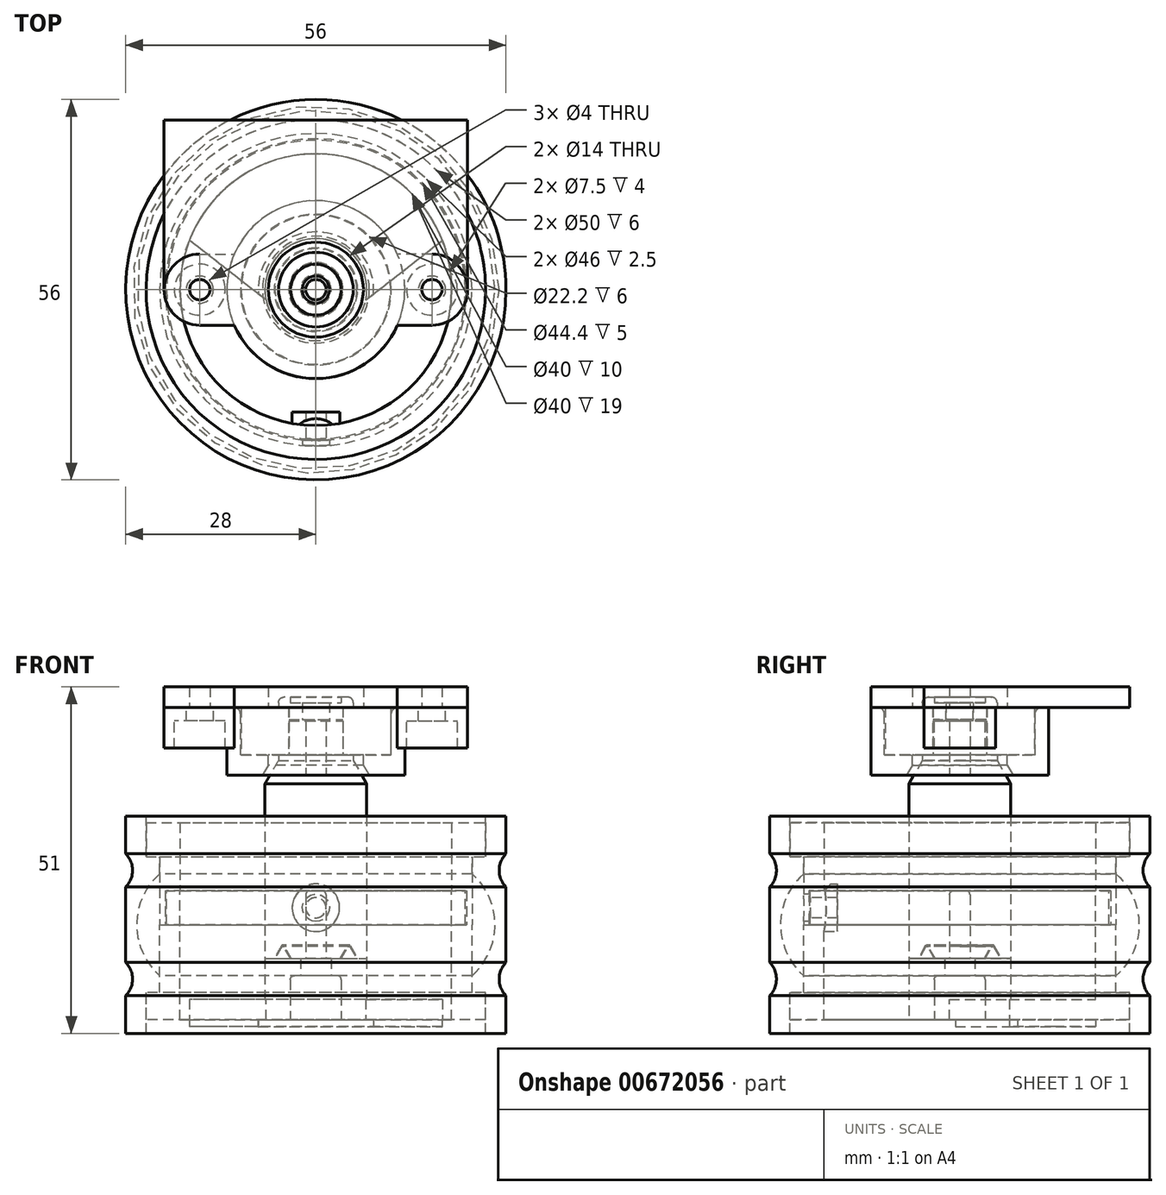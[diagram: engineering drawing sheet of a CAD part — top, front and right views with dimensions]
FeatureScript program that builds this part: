
annotation { "Feature Type Name" : "Feature", "Feature Type Description" : "" }
export const myFeature = defineFeature(function(context is Context, id is Id, definition is map)
    precondition{}
    {
        {
            var Q0;
            Q0=qCreatedBy(makeId("Top.planeOp"),FACE);
            var sketch = newSketch(context, id + "F0", { "sketchPlane" : qUnion([Q0])});
            skCircle(sketch, "E0", {"center": v(0, 0) * mm, "radius": 11.07 * mm});
            skCircle(sketch, "E1", {"center": v(0, 0) * mm, "radius": 13.75 * mm});
            skCircle(sketch, "E2", {"center": v(0, 0) * mm, "radius": 20 * mm});
            skCircle(sketch, "E3", {"center": v(0, 0) * mm, "radius": 25 * mm});
            skCircle(sketch, "E4", {"center": v(0, 0) * mm, "radius": 7.5 * mm});
            skSolve(sketch);
        }
        {
            var Q0;
            Q0=qCreatedBy(makeId("Front.planeOp"),FACE);
            var sketch = newSketch(context, id + "F1", { "sketchPlane" : qUnion([Q0])});
            skPoint(sketch, "E5.0", {"position": v(0, 0) * mm});
            skLineSegment(sketch, "E6", {"start": v(20, 30) * mm, "end": v(20, 0) * mm, "construction": true});
            skLineSegment(sketch, "E7", {"start": v(25, 30) * mm, "end": v(25, 0) * mm, "construction": true});
            skLineSegment(sketch, "E8", {"start": v(25, 30) * mm, "end": v(25, 25) * mm});
            skLineSegment(sketch, "E9", {"start": v(25, 25) * mm, "end": v(23, 25) * mm});
            skLineSegment(sketch, "E10", {"start": v(23, 25) * mm, "end": v(23, 15) * mm});
            skLineSegment(sketch, "E11", {"start": v(25, 30) * mm, "end": v(20, 30) * mm});
            skLineSegment(sketch, "E12", {"start": v(20, 15) * mm, "end": v(20, 30) * mm});
            skLineSegment(sketch, "E13", {"start": v(20, 15) * mm, "end": v(23, 15) * mm});
            skLineSegment(sketch, "E14.MirrorCS", {"start": v(23, 5) * mm, "end": v(23, 15) * mm});
            skLineSegment(sketch, "E15.MirrorCS", {"start": v(25, 0) * mm, "end": v(25, 5) * mm});
            skLineSegment(sketch, "E16.MirrorCS", {"start": v(25, 5) * mm, "end": v(23, 5) * mm});
            skLineSegment(sketch, "E17.MirrorCS", {"start": v(25, 0) * mm, "end": v(20, 0) * mm});
            skLineSegment(sketch, "E18.MirrorCS", {"start": v(20, 15) * mm, "end": v(20, 0) * mm});
            skLineSegment(sketch, "E19", {"start": v(25, 25) * mm, "end": v(25, 5) * mm});
            skSolve(sketch);
        }
        {
            var Q0;
            Q0=qCreatedBy(makeId("Front.planeOp"),FACE);
            var sketch = newSketch(context, id + "F2", { "sketchPlane" : qUnion([Q0])});
            skLineSegment(sketch, "E20.0.0", {"start": v(23, 15) * mm, "end": v(20, 15) * mm});
            skLineSegment(sketch, "E20.0.1", {"start": v(20, 15) * mm, "end": v(20, 0) * mm});
            skLineSegment(sketch, "E20.0.2", {"start": v(20, 0) * mm, "end": v(25, 0) * mm});
            skLineSegment(sketch, "E20.0.3", {"start": v(25, 0) * mm, "end": v(25, 5) * mm});
            skLineSegment(sketch, "E20.0.4", {"start": v(25, 5) * mm, "end": v(23, 5) * mm});
            skLineSegment(sketch, "E20.0.5", {"start": v(23, 5) * mm, "end": v(23, 15) * mm});
            skLineSegment(sketch, "E21", {"start": v(20, 15) * mm, "end": v(20, 20) * mm});
            skLineSegment(sketch, "E22", {"start": v(20, 20) * mm, "end": v(22, 20) * mm});
            skLineSegment(sketch, "E23", {"start": v(22, 20) * mm, "end": v(22, 15) * mm});
            skSolve(sketch);
        }
        {
            var Q0;
            Q0=qCreatedBy(makeId("Front.planeOp"),FACE);
            var sketch = newSketch(context, id + "F3", { "sketchPlane" : qUnion([Q0])});
            skLineSegment(sketch, "E24.0.0", {"start": v(20, 30) * mm, "end": v(20, 15) * mm});
            skLineSegment(sketch, "E24.0.1", {"start": v(20, 15) * mm, "end": v(23, 15) * mm});
            skLineSegment(sketch, "E24.0.2", {"start": v(23, 15) * mm, "end": v(23, 25) * mm});
            skLineSegment(sketch, "E24.0.3", {"start": v(23, 25) * mm, "end": v(25, 25) * mm});
            skLineSegment(sketch, "E24.0.4", {"start": v(25, 25) * mm, "end": v(25, 30) * mm});
            skLineSegment(sketch, "E24.0.5", {"start": v(25, 30) * mm, "end": v(20, 30) * mm});
            skLineSegment(sketch, "E25.0", {"start": v(22.2, 20) * mm, "end": v(22.2, 15) * mm});
            skLineSegment(sketch, "E26.0", {"start": v(20, 20) * mm, "end": v(22, 20) * mm, "construction": true});
            skLineSegment(sketch, "E27", {"start": v(20, 20) * mm, "end": v(22.2, 20) * mm});
            skSolve(sketch);
        }
        {
            var Q0;
            Q0=qCreatedBy(makeId("Top.planeOp"),FACE);
            var sketch = newSketch(context, id + "F4", { "sketchPlane" : qUnion([Q0])});
            skCircle(sketch, "E28", {"center": v(0, 0) * mm, "radius": 2.25 * mm});
            skCircle(sketch, "E29", {"center": v(0, 0) * mm, "radius": 3.75 * mm});
            skCircle(sketch, "E30", {"center": v(0, 0) * mm, "radius": 7.5 * mm});
            skSolve(sketch);
        }
        {
            var Q0;
            Q0=makeQuery(id+"F4.imprint","IMPRINT",FACE,{"disambiguationData":[TD([[makeQuery(id+"F4.imprint","IMPRINT",EDGE,{"derivedFrom":sQuery(id+"F4.wireOp",EDGE,"E29")}),-1.0]])]});
            var Q1;
            Q1=makeQuery(id+"F4.imprint","IMPRINT",FACE,{"disambiguationData":[TD([[makeQuery(id+"F4.imprint","IMPRINT",EDGE,{"derivedFrom":sQuery(id+"F4.wireOp",EDGE,"E28")}),-1.0]])]});
            extrude(context, id + "F5", {"entities" : qUnion([Q0, Q1]), "depth" : 10 * mm, "offsetDistance" : 25 * mm});
        }
        {
            var Q0;
            Q0=makeQuery(id+"F4.imprint","IMPRINT",FACE,{"disambiguationData":[TD([[makeQuery(id+"F4.imprint","IMPRINT",EDGE,{"derivedFrom":sQuery(id+"F4.wireOp",EDGE,"E28")}),-1.0]])]});
            extrude(context, id + "F6", {"entities" : qUnion([Q0]), "operationType" : NewBodyOperationType.REMOVE, "depth" : 7.5 * mm, "offsetDistance" : 25 * mm});
        }
        {
            var Q0;
            Q0=qCreatedBy(makeId("Front.planeOp"),FACE);
            var sketch = newSketch(context, id + "F7", { "sketchPlane" : qUnion([Q0])});
            skLineSegment(sketch, "E31.0.0", {"start": v(-7.5, 10) * mm, "end": v(7.5, 10) * mm});
            skLineSegment(sketch, "E32.0", {"start": v(-20, 0) * mm, "end": v(20, 0) * mm});
            skLineSegment(sketch, "E33", {"start": v(-7.5, 0) * mm, "end": v(-7.5, 10) * mm});
            skLineSegment(sketch, "E34", {"start": v(7.5, 10) * mm, "end": v(7.5, 0) * mm});
            skLineSegment(sketch, "E35", {"start": v(-2.25, 7.5) * mm, "end": v(-2.25, 10) * mm});
            skLineSegment(sketch, "E36", {"start": v(2.25, 10) * mm, "end": v(2.25, 7.5) * mm});
            skLineSegment(sketch, "E37", {"start": v(-2.25, 10) * mm, "end": v(-7.5, 10) * mm});
            skLineSegment(sketch, "E38", {"start": v(-4.88, 10) * mm, "end": v(-4.88, 12) * mm, "construction": true});
            skLineSegment(sketch, "E39", {"start": v(-4.88, 12) * mm, "end": v(-6.03, 10) * mm});
            skLineSegment(sketch, "E40.MirrorCS", {"start": v(-4.88, 12) * mm, "end": v(-3.72, 10) * mm});
            skSolve(sketch);
        }
        {
            var Q0;
            {var subQ0=sQuery(id+"F7.wireOp",EDGE,"E39");Q0=makeQuery(id+"F7.imprint","IMPRINT",FACE,{"disambiguationData":[TD([[makeQuery(id+"F7.imprint","IMPRINT",EDGE,{"derivedFrom":subQ0}),1.0]])]});}
            var Q1;
            Q1=makeQuery(id+"F5.opExtrude","SWEPT_FACE",FACE,{"disambiguationData":[OSD([sQuery(id+"F4.wireOp",EDGE,"E28")])]});
            revolve(context, id + "F8", {"operationType" : NewBodyOperationType.ADD, "entities" : qUnion([Q0]), "axis" : qUnion([Q1]), "revolveType" : RevolveType.FULL});
        }
        {
            var Q0;
            Q0=qCreatedBy(makeId("Front.planeOp"),FACE);
            var sketch = newSketch(context, id + "F9", { "sketchPlane" : qUnion([Q0])});
            skLineSegment(sketch, "E41.0", {"start": v(-7.5, 10) * mm, "end": v(7.5, 10) * mm});
            skLineSegment(sketch, "E42", {"start": v(0, 0) * mm, "end": v(0, 10) * mm, "construction": true});
            skLineSegment(sketch, "E43", {"start": v(0, 10) * mm, "end": v(0, 45) * mm});
            skLineSegment(sketch, "E44", {"start": v(7.5, 10) * mm, "end": v(7.5, 45) * mm});
            skLineSegment(sketch, "E45", {"start": v(7.5, 45) * mm, "end": v(0, 45) * mm});
            skLineSegment(sketch, "E46", {"start": v(7.5, 45) * mm, "end": v(7.5, 40) * mm, "construction": true});
            skLineSegment(sketch, "E47", {"start": v(7.5, 40) * mm, "end": v(0, 40) * mm, "construction": true});
            skLineSegment(sketch, "E48", {"start": v(0, 40) * mm, "end": v(3.95, 40) * mm, "construction": true});
            skLineSegment(sketch, "E49", {"start": v(3.95, 40) * mm, "end": v(3.95, 45) * mm});
            skLineSegment(sketch, "E50", {"start": v(3.95, 40) * mm, "end": v(7.5, 40) * mm});
            skLineSegment(sketch, "E51", {"start": v(0, 10) * mm, "end": v(0, 20) * mm, "construction": true});
            skLineSegment(sketch, "E52", {"start": v(0, 20) * mm, "end": v(1.5, 20) * mm});
            skLineSegment(sketch, "E53", {"start": v(1.5, 20) * mm, "end": v(1.5, 10) * mm});
            skLineSegment(sketch, "E54", {"start": v(1.5, 10) * mm, "end": v(0, 10) * mm});
            skLineSegment(sketch, "E55", {"start": v(0, 45) * mm, "end": v(1.5, 45) * mm});
            skLineSegment(sketch, "E56", {"start": v(1.5, 45) * mm, "end": v(1.5, 40) * mm});
            skLineSegment(sketch, "E57", {"start": v(1.5, 40) * mm, "end": v(0, 40) * mm});
            skLineSegment(sketch, "E58", {"start": v(4.88, 12) * mm, "end": v(3.72, 10) * mm});
            skLineSegment(sketch, "E59", {"start": v(-6.03, 10) * mm, "end": v(-4.88, 12) * mm});
            skLineSegment(sketch, "E60", {"start": v(4.88, 12) * mm, "end": v(6.03, 10) * mm});
            skLineSegment(sketch, "E61.0.0", {"start": v(-3.72, 10) * mm, "end": v(3.72, 10) * mm});
            skLineSegment(sketch, "E62.0", {"start": v(4.88, 12.2) * mm, "end": v(3.6, 10) * mm});
            skLineSegment(sketch, "E62.1", {"start": v(4.88, 12.2) * mm, "end": v(6.15, 10) * mm});
            skLineSegment(sketch, "E63", {"start": v(7.5, 45) * mm, "end": v(7.5, 45.2) * mm, "construction": true});
            skLineSegment(sketch, "E64", {"start": v(7.5, 45.2) * mm, "end": v(0, 45.2) * mm, "construction": true});
            skLineSegment(sketch, "E65", {"start": v(0, 40) * mm, "end": v(5.5, 40) * mm});
            skLineSegment(sketch, "E66", {"start": v(5.5, 40) * mm, "end": v(5.5, 39.2) * mm});
            skLineSegment(sketch, "E67", {"start": v(5.5, 39.2) * mm, "end": v(7.5, 39.2) * mm});
            skLineSegment(sketch, "E68", {"start": v(3.95, 45) * mm, "end": v(3.95, 45.2) * mm, "construction": true});
            skLineSegment(sketch, "E69", {"start": v(3.95, 45.2) * mm, "end": v(3.95, 47) * mm});
            skLineSegment(sketch, "E70", {"start": v(5.5, 40) * mm, "end": v(5.5, 47) * mm, "construction": true});
            skLineSegment(sketch, "E71", {"start": v(5.5, 47) * mm, "end": v(3.95, 47) * mm});
            skLineSegment(sketch, "E72", {"start": v(5.5, 47) * mm, "end": v(5.5, 48.5) * mm});
            skLineSegment(sketch, "E73", {"start": v(5.5, 48.5) * mm, "end": v(0, 48.5) * mm});
            skLineSegment(sketch, "E74", {"start": v(0, 48.5) * mm, "end": v(0, 45.2) * mm});
            skLineSegment(sketch, "E75", {"start": v(3.95, 45.2) * mm, "end": v(0, 45.2) * mm});
            skLineSegment(sketch, "E76", {"start": v(0, 48.5) * mm, "end": v(1.88, 48.5) * mm});
            skLineSegment(sketch, "E77", {"start": v(0, 45.2) * mm, "end": v(2, 45.2) * mm, "construction": true});
            skLineSegment(sketch, "E78", {"start": v(2, 45.2) * mm, "end": v(2, 47.7) * mm});
            skLineSegment(sketch, "E79", {"start": v(0, 48.5) * mm, "end": v(3.75, 48.5) * mm, "construction": true});
            skLineSegment(sketch, "E80", {"start": v(3.75, 48.5) * mm, "end": v(3.75, 47.7) * mm});
            skLineSegment(sketch, "E81", {"start": v(3.75, 47.7) * mm, "end": v(2, 47.7) * mm});
            skLineSegment(sketch, "E82", {"start": v(5.5, 39.2) * mm, "end": v(7.5, 35.74) * mm});
            skLineSegment(sketch, "E83", {"start": v(1.5, 40) * mm, "end": v(1.5, 37) * mm});
            skLineSegment(sketch, "E84", {"start": v(1.5, 37) * mm, "end": v(0, 37) * mm});
            skSolve(sketch);
        }
        {
            var Q0;
            {var subQ4=sQuery(id+"F9.wireOp",EDGE,"E52");Q0=makeQuery(id+"F9.imprint","IMPRINT",FACE,{"disambiguationData":[TD([[makeQuery(id+"F9.imprint","IMPRINT",EDGE,{"derivedFrom":subQ4}),1.0]])]});}
            var Q1;
            {var subQ2=sQuery(id+"F9.wireOp",EDGE,"E49");Q1=makeQuery(id+"F9.imprint","IMPRINT",FACE,{"disambiguationData":[TD([[makeQuery(id+"F9.imprint","IMPRINT",EDGE,{"derivedFrom":subQ2}),1.0]])]});}
            var Q2;
            {var subQ3=sQuery(id+"F9.wireOp",EDGE,"E69");Q2=makeQuery(id+"F9.imprint","IMPRINT",FACE,{"disambiguationData":[TD([[makeQuery(id+"F9.imprint","IMPRINT",EDGE,{"derivedFrom":subQ3}),1.0]])]});}
            var Q3;
            Q3=sQuery(id+"F9.wireOp",EDGE,"E43");
            revolve(context, id + "F10", {"entities" : qUnion([Q0, Q1, Q2]), "axis" : qUnion([Q3]), "revolveType" : RevolveType.FULL});
        }
        {
            var Q0;
            Q0=makeQuery(id+"F8.opRevolve","SWEPT_EDGE",EDGE,{"disambiguationData":[OSD([sQuery(id+"F7.wireOp",EDGE,"E39"),sQuery(id+"F7.wireOp",EDGE,"E40.MirrorCS")])]});
            var Q1;
            Q1=makeQuery(id+"F10.opRevolve","SWEPT_EDGE",EDGE,{"disambiguationData":[OSD([sQuery(id+"F9.wireOp",EDGE,"E62.0"),sQuery(id+"F9.wireOp",EDGE,"E62.1")])]});
            fillet(context, id + "F11", {"entities" : qUnion([Q0, Q1]), "radius" : .2 * mm, "tangentPropagation" : true, "allowEdgeOverflow" : false});
        }
        {
            var Q0;
            Q0=makeQuery(id+"F10.opRevolve","SWEPT_EDGE",EDGE,{"disambiguationData":[OSD([sQuery(id+"F9.wireOp",EDGE,"E52"),sQuery(id+"F9.wireOp",EDGE,"E53")])]});
            var Q1;
            Q1=makeQuery(id+"F6.boolean.opBoolean","COPY",EDGE,{"derivedFrom":makeQuery(id+"F6.opExtrude","CAP_EDGE",EDGE,{"disambiguationData":[OSD([sQuery(id+"F4.wireOp",EDGE,"E28")])],"isStart":false})});
            var Q2;
            Q2=makeQuery(id+"F6.boolean.opBoolean","COPY",EDGE,{"derivedFrom":makeQuery(id+"F6.opExtrude","CAP_EDGE",EDGE,{"disambiguationData":[OSD([sQuery(id+"F4.wireOp",EDGE,"E29")])],"isStart":false})});
            fillet(context, id + "F12", {"entities" : qUnion([Q0, Q1, Q2]), "radius" : .6 * mm, "tangentPropagation" : true, "allowEdgeOverflow" : false});
        }
        {
            var Q0;
            Q0=makeQuery(id+"F10.opRevolve","SWEPT_EDGE",EDGE,{"disambiguationData":[OSD([sQuery(id+"F9.wireOp",EDGE,"E72"),sQuery(id+"F9.wireOp",EDGE,"E73")])]});
            fillet(context, id + "F13", {"entities" : qUnion([Q0]), "radius" : .8 * mm, "tangentPropagation" : true, "allowEdgeOverflow" : false});
        }
        {
            var Q0;
            Q0=qCreatedBy(makeId("Front.planeOp"),FACE);
            var sketch = newSketch(context, id + "F14", { "sketchPlane" : qUnion([Q0])});
            skLineSegment(sketch, "E85.0.0", {"start": v(-5.5, 40) * mm, "end": v(5.5, 40) * mm, "construction": true});
            skLineSegment(sketch, "E86", {"start": v(-3.95, 40) * mm, "end": v(-3.95, 45) * mm, "construction": true});
            skLineSegment(sketch, "E87", {"start": v(3.95, 45) * mm, "end": v(3.95, 40) * mm, "construction": true});
            skLineSegment(sketch, "E88.0.0", {"start": v(5.5, 47) * mm, "end": v(-5.5, 47) * mm, "construction": true});
            skLineSegment(sketch, "E89", {"start": v(-3.95, 45.2) * mm, "end": v(-3.95, 47) * mm, "construction": true});
            skLineSegment(sketch, "E90", {"start": v(3.95, 47) * mm, "end": v(3.95, 45.2) * mm, "construction": true});
            skLineSegment(sketch, "E91", {"start": v(-5.5, 47) * mm, "end": v(-5.5, 40) * mm});
            skLineSegment(sketch, "E92", {"start": v(0, 40) * mm, "end": v(0, 47) * mm, "construction": true});
            skLineSegment(sketch, "E93", {"start": v(0, 43.5) * mm, "end": v(-11, 43.5) * mm, "construction": true});
            skLineSegment(sketch, "E94", {"start": v(-11, 43.5) * mm, "end": v(-11, 47) * mm});
            skLineSegment(sketch, "E95", {"start": v(-11, 47) * mm, "end": v(-5.5, 47) * mm});
            skLineSegment(sketch, "E96", {"start": v(-11, 43.5) * mm, "end": v(-11, 40) * mm});
            skLineSegment(sketch, "E97", {"start": v(-11, 40) * mm, "end": v(-5.5, 40) * mm});
            skLineSegment(sketch, "E98", {"start": v(-3.95, 40) * mm, "end": v(-3.95, 47) * mm});
            skLineSegment(sketch, "E99", {"start": v(0, 43.5) * mm, "end": v(-4, 43.5) * mm, "construction": true});
            skLineSegment(sketch, "E100", {"start": v(-4, 43.5) * mm, "end": v(-4, 47) * mm});
            skLineSegment(sketch, "E101", {"start": v(-4, 47) * mm, "end": v(-5.5, 47) * mm});
            skLineSegment(sketch, "E102", {"start": v(-4, 43.5) * mm, "end": v(-4, 40) * mm});
            skLineSegment(sketch, "E103", {"start": v(-4, 40) * mm, "end": v(-5.5, 40) * mm});
            skSolve(sketch);
        }
        {
            var Q0;
            Q0=makeQuery(id+"F14.imprint","IMPRINT",FACE,{"disambiguationData":[TD([[makeQuery(id+"F14.imprint","IMPRINT",EDGE,{"derivedFrom":sQuery(id+"F14.wireOp",EDGE,"E91")}),-1.0]])]});
            var Q1;
            Q1=makeQuery(id+"F14.imprint","IMPRINT",FACE,{"disambiguationData":[TD([[makeQuery(id+"F14.imprint","IMPRINT",EDGE,{"derivedFrom":sQuery(id+"F14.wireOp",EDGE,"E91")}),1.0]])]});
            var Q2;
            Q2=sQuery(id+"F14.wireOp",EDGE,"E92");
            revolve(context, id + "F15", {"entities" : qUnion([Q0, Q1]), "axis" : qUnion([Q2]), "revolveType" : RevolveType.FULL});
        }
        {
            var Q0;
            Q0=qCreatedBy(makeId("Front.planeOp"),FACE);
            var sketch = newSketch(context, id + "F16", { "sketchPlane" : qUnion([Q0])});
            skLineSegment(sketch, "E104", {"start": v(-1.5, 40) * mm, "end": v(-1.5, 45) * mm, "construction": true});
            skLineSegment(sketch, "E105", {"start": v(1.5, 45) * mm, "end": v(1.5, 40) * mm, "construction": true});
            skLineSegment(sketch, "E106.0.0", {"start": v(3.95, 40) * mm, "end": v(-3.95, 40) * mm, "construction": true});
            skLineSegment(sketch, "E107.0.0", {"start": v(-3.95, 45) * mm, "end": v(3.95, 45) * mm, "construction": true});
            skLineSegment(sketch, "E108", {"start": v(0, 45) * mm, "end": v(0, 40) * mm, "construction": true});
            skLineSegment(sketch, "E109.0.0", {"start": v(11, 40) * mm, "end": v(-11, 40) * mm, "construction": true});
            skLineSegment(sketch, "E110", {"start": v(-11, 40) * mm, "end": v(-11, 47) * mm, "construction": true});
            skLineSegment(sketch, "E111", {"start": v(11, 47) * mm, "end": v(11, 40) * mm, "construction": true});
            skLineSegment(sketch, "E112", {"start": v(-7.5, 35.74) * mm, "end": v(-5.5, 39.2) * mm, "construction": true});
            skLineSegment(sketch, "E113", {"start": v(5.5, 39.2) * mm, "end": v(7.5, 35.74) * mm, "construction": true});
            skLineSegment(sketch, "E114", {"start": v(-5.5, 39.2) * mm, "end": v(-5.5, 40) * mm, "construction": true});
            skLineSegment(sketch, "E115", {"start": v(5.5, 40) * mm, "end": v(5.5, 39.2) * mm, "construction": true});
            skLineSegment(sketch, "E116", {"start": v(-5.5, 40) * mm, "end": v(-7, 40) * mm, "construction": true});
            skLineSegment(sketch, "E117", {"start": v(-7, 40) * mm, "end": v(-7, 38.5) * mm});
            skLineSegment(sketch, "E118", {"start": v(0, 40) * mm, "end": v(-11.1, 40) * mm});
            skLineSegment(sketch, "E119", {"start": v(-11.1, 40) * mm, "end": v(-11.1, 47.44) * mm});
            skLineSegment(sketch, "E120", {"start": v(-11.1, 47) * mm, "end": v(-13.1, 47) * mm});
            skLineSegment(sketch, "E121", {"start": v(-7, 38.5) * mm, "end": v(-7.87, 37) * mm});
            skLineSegment(sketch, "E122", {"start": v(-7.87, 37) * mm, "end": v(-13.1, 37) * mm});
            skLineSegment(sketch, "E123", {"start": v(-13.1, 37) * mm, "end": v(-13.1, 47) * mm});
            skLineSegment(sketch, "E124", {"start": v(-13.1, 47) * mm, "end": v(-21.1, 47) * mm});
            skLineSegment(sketch, "E125", {"start": v(-21.1, 47) * mm, "end": v(-21.1, 44) * mm});
            skLineSegment(sketch, "E126", {"start": v(-21.1, 44) * mm, "end": v(-13.1, 44) * mm});
            skSolve(sketch);
        }
        {
            var Q0;
            {var subQ4=sQuery(id+"F16.wireOp",EDGE,"E117");Q0=makeQuery(id+"F16.imprint","IMPRINT",FACE,{"disambiguationData":[TD([[makeQuery(id+"F16.imprint","IMPRINT",EDGE,{"derivedFrom":subQ4}),-1.0]])]});}
            var Q1;
            Q1=sQuery(id+"F16.wireOp",EDGE,"E108");
            revolve(context, id + "F17", {"entities" : qUnion([Q0]), "axis" : qUnion([Q1]), "revolveType" : RevolveType.FULL});
        }
        {
            var Q0;
            Q0=makeQuery(id+"F17.opRevolve","SWEPT_FACE",FACE,{"disambiguationData":[OSD([sQuery(id+"F16.wireOp",EDGE,"E120")])]});
            var sketch = newSketch(context, id + "F18", { "sketchPlane" : qUnion([Q0])});
            skCircle(sketch, "E127.0", {"center": v(0, 0) * mm, "radius": 13.1 * mm, "construction": true});
            skLineSegment(sketch, "E128.0", {"start": v(-21.1, 0) * mm, "end": v(-13.1, 0) * mm, "construction": true});
            skCircle(sketch, "E129", {"center": v(-17.1, 0) * mm, "radius": 3.75 * mm});
            skCircle(sketch, "E130", {"center": v(-17.1, 0) * mm, "radius": 2 * mm});
            skCircle(sketch, "E131", {"center": v(-17.1, 0) * mm, "radius": 5.25 * mm});
            skLineSegment(sketch, "E132", {"start": v(-17.1, 0) * mm, "end": v(-17.1, 5.25) * mm, "construction": true});
            skLineSegment(sketch, "E133", {"start": v(-17.1, 0) * mm, "end": v(-17.1, -5.25) * mm, "construction": true});
            skLineSegment(sketch, "E134", {"start": v(-17.1, -5.25) * mm, "end": v(-12, -5.25) * mm});
            skLineSegment(sketch, "E135", {"start": v(-17.1, 5.25) * mm, "end": v(-12, 5.25) * mm});
            skLineSegment(sketch, "E136", {"start": v(0, 0) * mm, "end": v(0, 7.47) * mm});
            skCircle(sketch, "E137.MirrorC", {"center": v(17.1, 0) * mm, "radius": 5.25 * mm});
            skCircle(sketch, "E138.MirrorC", {"center": v(17.1, 0) * mm, "radius": 2 * mm});
            skCircle(sketch, "E139.MirrorC", {"center": v(17.1, 0) * mm, "radius": 3.75 * mm});
            skLineSegment(sketch, "E140.MirrorCS", {"start": v(17.1, 5.25) * mm, "end": v(12, 5.25) * mm});
            skLineSegment(sketch, "E141.MirrorCS", {"start": v(17.1, -5.25) * mm, "end": v(12, -5.25) * mm});
            skSolve(sketch);
        }
        {
            var Q0;
            Q0=makeQuery(id+"F18.imprint","IMPRINT",FACE,{"disambiguationData":[TD([[makeQuery(id+"F18.imprint","IMPRINT",EDGE,{"derivedFrom":sQuery(id+"F18.wireOp",EDGE,"E129")}),1.0]])]});
            var Q1;
            Q1=makeQuery(id+"F18.imprint","IMPRINT",FACE,{"disambiguationData":[TD([[makeQuery(id+"F18.imprint","IMPRINT",EDGE,{"derivedFrom":sQuery(id+"F18.wireOp",EDGE,"E129")}),-1.0]])]});
            var Q2;
            {var subQ0=sQuery(id+"F18.wireOp",EDGE,"E134");Q2=makeQuery(id+"F18.imprint","IMPRINT",FACE,{"disambiguationData":[TD([[makeQuery(id+"F18.imprint","IMPRINT",EDGE,{"derivedFrom":subQ0}),1.0]])]});}
            var Q3;
            {var subQ0=sQuery(id+"F18.wireOp",EDGE,"E135");Q3=makeQuery(id+"F18.imprint","IMPRINT",FACE,{"disambiguationData":[TD([[makeQuery(id+"F18.imprint","IMPRINT",EDGE,{"derivedFrom":subQ0}),-1.0]])]});}
            extrude(context, id + "F19", {"entities" : qUnion([Q0, Q1, Q2, Q3]), "oppositeDirection" : true, "depth" : 2 * mm, "offsetDistance" : 25 * mm});
        }
        {
            var Q0;
            Q0=makeQuery(id+"F18.imprint","IMPRINT",FACE,{"disambiguationData":[TD([[makeQuery(id+"F18.imprint","IMPRINT",EDGE,{"derivedFrom":sQuery(id+"F18.wireOp",EDGE,"E129")}),-1.0]])]});
            var Q1;
            {var subQ0=sQuery(id+"F18.wireOp",EDGE,"E135");Q1=makeQuery(id+"F18.imprint","IMPRINT",FACE,{"disambiguationData":[TD([[makeQuery(id+"F18.imprint","IMPRINT",EDGE,{"derivedFrom":subQ0}),-1.0]])]});}
            var Q2;
            {var subQ0=sQuery(id+"F18.wireOp",EDGE,"E134");Q2=makeQuery(id+"F18.imprint","IMPRINT",FACE,{"disambiguationData":[TD([[makeQuery(id+"F18.imprint","IMPRINT",EDGE,{"derivedFrom":subQ0}),1.0]])]});}
            extrude(context, id + "F20", {"entities" : qUnion([Q0, Q1, Q2]), "oppositeDirection" : true, "depth" : 6 * mm, "offsetDistance" : 25 * mm});
        }
        {
            var Q0;
            Q0=makeQuery(id+"F20.opExtrude","SWEPT_BODY",BODY,{"disambiguationData":[OSD([sQuery(id+"F16.wireOp",EDGE,"E120"),sQuery(id+"F16.wireOp",EDGE,"E123"),sQuery(id+"F16.wireOp",EDGE,"E124"),sQuery(id+"F18.wireOp",EDGE,"E129"),sQuery(id+"F18.wireOp",EDGE,"E131"),sQuery(id+"F18.wireOp",EDGE,"E134"),sQuery(id+"F18.wireOp",EDGE,"E135")])]});
            var Q1;
            Q1=makeQuery(id+"F19.opExtrude","SWEPT_BODY",BODY,{"disambiguationData":[OSD([sQuery(id+"F16.wireOp",EDGE,"E120"),sQuery(id+"F16.wireOp",EDGE,"E123"),sQuery(id+"F16.wireOp",EDGE,"E124"),sQuery(id+"F18.wireOp",EDGE,"E130"),sQuery(id+"F18.wireOp",EDGE,"E131"),sQuery(id+"F18.wireOp",EDGE,"E134"),sQuery(id+"F18.wireOp",EDGE,"E135")])]});
            booleanBodies(context, id + "F21", {"operationType" : BooleanOperationType.UNION, "tools" : qUnion([Q0, Q1])});
        }
        {
            var Q0;
            Q0=makeQuery(id+"F20.opExtrude","SWEPT_BODY",BODY,{"disambiguationData":[OSD([sQuery(id+"F16.wireOp",EDGE,"E120"),sQuery(id+"F16.wireOp",EDGE,"E123"),sQuery(id+"F16.wireOp",EDGE,"E124"),sQuery(id+"F18.wireOp",EDGE,"E129"),sQuery(id+"F18.wireOp",EDGE,"E131"),sQuery(id+"F18.wireOp",EDGE,"E134"),sQuery(id+"F18.wireOp",EDGE,"E135")])]});
            var Q1;
            Q1=sQuery(id+"F16.wireOp",EDGE,"E108");
            circularPattern(context, id + "F22", {"entities" : qUnion([Q0]), "axis" : qUnion([Q1]), "angle" : 360 * degree, "instanceCount" : 2, "equalSpace" : true});
        }
        {
            var Q0;
            Q0=makeQuery(id+"F17.opRevolve","SWEPT_BODY",BODY,{"disambiguationData":[OSD([sQuery(id+"F16.wireOp",EDGE,"E117"),sQuery(id+"F16.wireOp",EDGE,"E118"),sQuery(id+"F16.wireOp",EDGE,"E119"),sQuery(id+"F16.wireOp",EDGE,"E120"),sQuery(id+"F16.wireOp",EDGE,"E121"),sQuery(id+"F16.wireOp",EDGE,"E122"),sQuery(id+"F16.wireOp",EDGE,"E123")])]});
            var Q1;
            Q1=makeQuery(id+"F20.opExtrude","SWEPT_BODY",BODY,{"disambiguationData":[OSD([sQuery(id+"F16.wireOp",EDGE,"E120"),sQuery(id+"F16.wireOp",EDGE,"E123"),sQuery(id+"F16.wireOp",EDGE,"E124"),sQuery(id+"F18.wireOp",EDGE,"E129"),sQuery(id+"F18.wireOp",EDGE,"E131"),sQuery(id+"F18.wireOp",EDGE,"E134"),sQuery(id+"F18.wireOp",EDGE,"E135")])]});
            var Q2;
            Q2=makeQuery(id+"F22.opPattern","COPY",BODY,{"derivedFrom":makeQuery(id+"F20.opExtrude","SWEPT_BODY",BODY,{"disambiguationData":[OSD([sQuery(id+"F16.wireOp",EDGE,"E120"),sQuery(id+"F16.wireOp",EDGE,"E123"),sQuery(id+"F16.wireOp",EDGE,"E124"),sQuery(id+"F18.wireOp",EDGE,"E129"),sQuery(id+"F18.wireOp",EDGE,"E131"),sQuery(id+"F18.wireOp",EDGE,"E134"),sQuery(id+"F18.wireOp",EDGE,"E135")])]}),"instanceName":"2"});
            var Q3;
            Q3=makeQuery(id+"F22.opPattern","COPY",BODY,{"derivedFrom":makeQuery(id+"F20.opExtrude","SWEPT_BODY",BODY,{"disambiguationData":[OSD([sQuery(id+"F16.wireOp",EDGE,"E120"),sQuery(id+"F16.wireOp",EDGE,"E123"),sQuery(id+"F16.wireOp",EDGE,"E124"),sQuery(id+"F18.wireOp",EDGE,"E129"),sQuery(id+"F18.wireOp",EDGE,"E131"),sQuery(id+"F18.wireOp",EDGE,"E134"),sQuery(id+"F18.wireOp",EDGE,"E135")])]}),"instanceName":"1"});
            booleanBodies(context, id + "F23", {"operationType" : BooleanOperationType.UNION, "tools" : qUnion([Q0, Q1, Q2, Q3])});
        }
        {
            var Q0;
            Q0=makeQuery(id+"F1.imprint","IMPRINT",FACE,{"disambiguationData":[TD([[makeQuery(id+"F1.imprint","IMPRINT",EDGE,{"derivedFrom":sQuery(id+"F1.wireOp",EDGE,"E15.MirrorCS")}),1.0]])]});
            var Q1;
            {var subQ0=sQuery(id+"F2.wireOp",EDGE,"E21");Q1=makeQuery(id+"F2.imprint","IMPRINT",FACE,{"disambiguationData":[TD([[makeQuery(id+"F2.imprint","IMPRINT",EDGE,{"derivedFrom":subQ0}),-1.0]])]});}
            var Q2;
            Q2=makeQuery(id+"F5.opExtrude","SWEPT_FACE",FACE,{"disambiguationData":[OSD([sQuery(id+"F4.wireOp",EDGE,"E30")])]});
            revolve(context, id + "F24", {"entities" : qUnion([Q0, Q1]), "axis" : qUnion([Q2]), "revolveType" : RevolveType.FULL});
        }
        {
            var Q0;
            Q0=makeQuery(id+"F24.opRevolve","SWEPT_BODY",BODY,{"disambiguationData":[OSD([sQuery(id+"F1.wireOp",EDGE,"E15.MirrorCS"),sQuery(id+"F1.wireOp",EDGE,"E16.MirrorCS"),sQuery(id+"F1.wireOp",EDGE,"E14.MirrorCS"),sQuery(id+"F1.wireOp",EDGE,"E17.MirrorCS"),sQuery(id+"F1.wireOp",EDGE,"E13"),sQuery(id+"F1.wireOp",EDGE,"E18.MirrorCS")])]});
            var Q1;
            Q1=makeQuery(id+"F24.opRevolve","SWEPT_BODY",BODY,{"disambiguationData":[OSD([sQuery(id+"F2.wireOp",EDGE,"E20.0.0"),sQuery(id+"F2.wireOp",EDGE,"E21"),sQuery(id+"F2.wireOp",EDGE,"E22"),sQuery(id+"F2.wireOp",EDGE,"E23")])]});
            booleanBodies(context, id + "F25", {"operationType" : BooleanOperationType.UNION, "tools" : qUnion([Q0, Q1])});
        }
        {
            var Q0;
            Q0=qCreatedBy(makeId("Front.planeOp"),FACE);
            cPlane(context, id + "F26", {"entities" : qUnion([Q0]), "cplaneType" : CPlaneType.OFFSET, "offset" : 25 * mm, "width" : 150 * mm, "height" : 150 * mm});
        }
        {
            var Q0;
            Q0=qCreatedBy(id+"F26.planeOp",FACE);
            var sketch = newSketch(context, id + "F27", { "sketchPlane" : qUnion([Q0])});
            skLineSegment(sketch, "E142.0", {"start": v(-22, 20) * mm, "end": v(22, 20) * mm, "construction": true});
            skLineSegment(sketch, "E143.0", {"start": v(-23, 15) * mm, "end": v(23, 15) * mm, "construction": true});
            skLineSegment(sketch, "E144", {"start": v(0, 15) * mm, "end": v(0, 20) * mm, "construction": true});
            skCircle(sketch, "E145", {"center": v(0, 17.5) * mm, "radius": 1.5 * mm});
            skCircle(sketch, "E146", {"center": v(0, 17.5) * mm, "radius": 2 * mm});
            skCircle(sketch, "E147", {"center": v(0, 17.5) * mm, "radius": 3.75 * mm});
            skSolve(sketch);
        }
        {
            var Q0;
            Q0=makeQuery(id+"F27.imprint","IMPRINT",FACE,{"disambiguationData":[TD([[makeQuery(id+"F27.imprint","IMPRINT",EDGE,{"derivedFrom":sQuery(id+"F27.wireOp",EDGE,"E145")}),1.0]])]});
            var Q1;
            Q1=makeQuery(id+"F10.opRevolve","SWEPT_FACE",FACE,{"disambiguationData":[OSD([sQuery(id+"F9.wireOp",EDGE,"E44")])]});
            extrude(context, id + "F28", {"entities" : qUnion([Q0]), "operationType" : NewBodyOperationType.REMOVE, "endBound" : BoundingType.UP_TO_SURFACE, "oppositeDirection" : true, "depth" : 25 * mm, "endBoundEntityFace" : qUnion([Q1]), "offsetDistance" : 25 * mm});
        }
        {
            var Q0;
            Q0=qCreatedBy(id+"F26.planeOp",FACE);
            cPlane(context, id + "F29", {"entities" : qUnion([Q0]), "cplaneType" : CPlaneType.OFFSET, "offset" : 7 * mm, "oppositeDirection" : true, "width" : 150 * mm, "height" : 150 * mm});
        }
        {
            var Q0;
            Q0=qCreatedBy(id+"F29.planeOp",FACE);
            var sketch = newSketch(context, id + "F30", { "sketchPlane" : qUnion([Q0])});
            skCircle(sketch, "E148.0", {"center": v(0, 17.5) * mm, "radius": 1.5 * mm});
            skCircle(sketch, "E149", {"center": v(0, 17.5) * mm, "radius": 3.5 * mm});
            skSolve(sketch);
        }
        {
            var Q0;
            Q0=makeQuery(id+"F30.imprint","IMPRINT",FACE,{"disambiguationData":[TD([[makeQuery(id+"F30.imprint","IMPRINT",EDGE,{"derivedFrom":sQuery(id+"F30.wireOp",EDGE,"E148.0")}),-1.0]])]});
            var Q1;
            Q1=makeQuery(id+"F25.opBoolean","MERGE",FACE,{"derivedFrom":[makeQuery(id+"F24.opRevolve","SWEPT_FACE",FACE,{"disambiguationData":[OSD([sQuery(id+"F1.wireOp",EDGE,"E18.MirrorCS")])]}),makeQuery(id+"F24.opRevolve","SWEPT_FACE",FACE,{"disambiguationData":[OSD([sQuery(id+"F2.wireOp",EDGE,"E21")])]})]});
            extrude(context, id + "F31", {"entities" : qUnion([Q0]), "operationType" : NewBodyOperationType.ADD, "endBound" : BoundingType.UP_TO_SURFACE, "depth" : 25 * mm, "endBoundEntityFace" : qUnion([Q1]), "offsetDistance" : 25 * mm});
        }
        {
            var Q0;
            Q0=qCreatedBy(makeId("Right.planeOp"),FACE);
            var sketch = newSketch(context, id + "F32", { "sketchPlane" : qUnion([Q0])});
            skLineSegment(sketch, "E150.0.0", {"start": v(-22, 20) * mm, "end": v(22, 20) * mm});
            skLineSegment(sketch, "E151", {"start": v(-20, 21) * mm, "end": v(-18, 21) * mm});
            skLineSegment(sketch, "E152", {"start": v(-20, 20) * mm, "end": v(-20, 21) * mm});
            skLineSegment(sketch, "E153", {"start": v(-20, 20) * mm, "end": v(-19, 21) * mm});
            skSolve(sketch);
        }
        {
            var Q0;
            {var subQ0=sQuery(id+"F32.wireOp",EDGE,"E152");Q0=makeQuery(id+"F32.imprint","IMPRINT",FACE,{"disambiguationData":[TD([[makeQuery(id+"F32.imprint","IMPRINT",EDGE,{"derivedFrom":subQ0}),-1.0]])]});}
            var Q1;
            Q1=makeQuery(id+"F25.opBoolean","MERGE",FACE,{"derivedFrom":[makeQuery(id+"F24.opRevolve","SWEPT_FACE",FACE,{"disambiguationData":[OSD([sQuery(id+"F1.wireOp",EDGE,"E18.MirrorCS")])]}),makeQuery(id+"F24.opRevolve","SWEPT_FACE",FACE,{"disambiguationData":[OSD([sQuery(id+"F2.wireOp",EDGE,"E21")])]})]});
            revolve(context, id + "F33", {"operationType" : NewBodyOperationType.REMOVE, "entities" : qUnion([Q0]), "axis" : qUnion([Q1]), "revolveType" : RevolveType.FULL, "oppositeDirection" : true});
        }
        {
            var Q0;
            {var subQ0=sQuery(id+"F3.wireOp",EDGE,"E24.0.2");Q0=makeQuery(id+"F3.imprint","IMPRINT",FACE,{"disambiguationData":[TD([[makeQuery(id+"F3.imprint","IMPRINT",EDGE,{"derivedFrom":subQ0}),1.0]])]});}
            var Q1;
            Q1=makeQuery(id+"F6.boolean.opBoolean","COPY",FACE,{"derivedFrom":makeQuery(id+"F6.opExtrude","SWEPT_FACE",FACE,{"disambiguationData":[OSD([sQuery(id+"F4.wireOp",EDGE,"E29")])]})});
            revolve(context, id + "F34", {"entities" : qUnion([Q0]), "axis" : qUnion([Q1]), "revolveType" : RevolveType.FULL});
        }
        {
            var Q0;
            Q0=qCreatedBy(id+"F26.planeOp",FACE);
            var sketch = newSketch(context, id + "F35", { "sketchPlane" : qUnion([Q0])});
            skCircle(sketch, "E154.0", {"center": v(0, 17.5) * mm, "radius": 2 * mm});
            skCircle(sketch, "E155.0", {"center": v(0, 17.5) * mm, "radius": 3.75 * mm});
            skSolve(sketch);
        }
        {
            var Q0;
            Q0=makeQuery(id+"F27.imprint","IMPRINT",FACE,{"disambiguationData":[TD([[makeQuery(id+"F27.imprint","IMPRINT",EDGE,{"derivedFrom":sQuery(id+"F27.wireOp",EDGE,"E145")}),-1.0]])]});
            var Q1;
            Q1=makeQuery(id+"F35.imprint","IMPRINT",FACE,{"disambiguationData":[TD([[makeQuery(id+"F35.imprint","IMPRINT",EDGE,{"derivedFrom":sQuery(id+"F35.wireOp",EDGE,"E154.0")}),1.0]])]});
            var Q2;
            Q2=makeQuery(id+"F24.opRevolve","SWEPT_FACE",FACE,{"disambiguationData":[OSD([sQuery(id+"F2.wireOp",EDGE,"E23")])]});
            var Q3;
            Q3=makeQuery(id+"F24.opRevolve","SWEPT_BODY",BODY,{"disambiguationData":[OSD([sQuery(id+"F1.wireOp",EDGE,"E15.MirrorCS"),sQuery(id+"F1.wireOp",EDGE,"E16.MirrorCS"),sQuery(id+"F1.wireOp",EDGE,"E14.MirrorCS"),sQuery(id+"F1.wireOp",EDGE,"E17.MirrorCS"),sQuery(id+"F1.wireOp",EDGE,"E13"),sQuery(id+"F1.wireOp",EDGE,"E18.MirrorCS")])]});
            extrude(context, id + "F36", {"entities" : qUnion([Q0, Q1]), "operationType" : NewBodyOperationType.REMOVE, "endBound" : BoundingType.UP_TO_SURFACE, "oppositeDirection" : true, "depth" : 25 * mm, "endBoundEntityFace" : qUnion([Q2]), "endBoundEntityBody" : qUnion([Q3]), "offsetDistance" : 25 * mm});
        }
        {
            var Q0;
            Q0=makeQuery(id+"F4.imprint","IMPRINT",FACE,{"disambiguationData":[TD([[makeQuery(id+"F4.imprint","IMPRINT",EDGE,{"derivedFrom":sQuery(id+"F4.wireOp",EDGE,"E29")}),-1.0]])]});
            var sketch = newSketch(context, id + "F37", { "sketchPlane" : qUnion([Q0])});
            skCircle(sketch, "E156.0", {"center": v(0, 0) * mm, "radius": 20 * mm});
            skCircle(sketch, "E157.0", {"center": v(0, 0) * mm, "radius": 7.5 * mm});
            skLineSegment(sketch, "E158", {"start": v(0, 0) * mm, "end": v(0, -20) * mm, "construction": true});
            skLineSegment(sketch, "E159", {"start": v(0, -20) * mm, "end": v(5, -20) * mm, "construction": true});
            skLineSegment(sketch, "E160", {"start": v(5, -19.36) * mm, "end": v(5, -5.6) * mm});
            skLineSegment(sketch, "E161.MirrorCS", {"start": v(-5, -19.36) * mm, "end": v(-5, -5.6) * mm});
            skPoint(sketch, "E162.orphan", {"position": v(-5, -20) * mm});
            skLineSegment(sketch, "E163.1.0", {"start": v(19.27, 5.35) * mm, "end": v(7.34, -1.54) * mm});
            skLineSegment(sketch, "E163.1.1", {"start": v(14.27, 14.01) * mm, "end": v(2.34, 7.13) * mm});
            skLineSegment(sketch, "E163.2.0", {"start": v(-14.27, 14.01) * mm, "end": v(-2.34, 7.13) * mm});
            skLineSegment(sketch, "E163.2.1", {"start": v(-19.27, 5.35) * mm, "end": v(-7.34, -1.54) * mm});
            skLineSegment(sketch, "E164", {"start": v(5, -5.6) * mm, "end": v(3, -19.77) * mm});
            skLineSegment(sketch, "E165.MirrorCS", {"start": v(-5, -5.6) * mm, "end": v(-3, -19.77) * mm});
            skLineSegment(sketch, "E166.1.0", {"start": v(7.34, -1.54) * mm, "end": v(18.63, 7.28) * mm});
            skLineSegment(sketch, "E166.1.1", {"start": v(2.34, 7.13) * mm, "end": v(15.62, 12.5) * mm});
            skLineSegment(sketch, "E166.2.0", {"start": v(-2.34, 7.13) * mm, "end": v(-15.62, 12.5) * mm});
            skLineSegment(sketch, "E166.2.1", {"start": v(-7.34, -1.54) * mm, "end": v(-18.63, 7.28) * mm});
            skSolve(sketch);
        }
        {
            var Q0;
            {var subQ0=sQuery(id+"F37.wireOp",EDGE,"E164");Q0=makeQuery(id+"F37.imprint","IMPRINT",FACE,{"disambiguationData":[TD([[makeQuery(id+"F37.imprint","IMPRINT",EDGE,{"derivedFrom":subQ0}),-1.0]])]});}
            var Q1;
            {var subQ0=sQuery(id+"F37.wireOp",EDGE,"E166.1.0");Q1=makeQuery(id+"F37.imprint","IMPRINT",FACE,{"disambiguationData":[TD([[makeQuery(id+"F37.imprint","IMPRINT",EDGE,{"derivedFrom":subQ0}),1.0]])]});}
            var Q2;
            {var subQ0=sQuery(id+"F37.wireOp",EDGE,"E166.2.0");Q2=makeQuery(id+"F37.imprint","IMPRINT",FACE,{"disambiguationData":[TD([[makeQuery(id+"F37.imprint","IMPRINT",EDGE,{"derivedFrom":subQ0}),1.0]])]});}
            extrude(context, id + "F38", {"entities" : qUnion([Q0, Q1, Q2]), "depth" : 4 * mm, "offsetDistance" : 25 * mm});
        }
        {
            var Q0;
            Q0=makeQuery(id+"F5.opExtrude","SWEPT_BODY",BODY,{"disambiguationData":[OSD([sQuery(id+"F4.wireOp",EDGE,"E28"),sQuery(id+"F4.wireOp",EDGE,"E30")])]});
            var Q1;
            Q1=makeQuery(id+"F38.opExtrude","SWEPT_BODY",BODY,{"disambiguationData":[OSD([sQuery(id+"F37.wireOp",EDGE,"E156.0"),sQuery(id+"F37.wireOp",EDGE,"E157.0"),sQuery(id+"F37.wireOp",EDGE,"E160"),sQuery(id+"F37.wireOp",EDGE,"E161.MirrorCS")])]});
            var Q2;
            Q2=makeQuery(id+"F38.opExtrude","SWEPT_BODY",BODY,{"disambiguationData":[OSD([sQuery(id+"F37.wireOp",EDGE,"E156.0"),sQuery(id+"F37.wireOp",EDGE,"E157.0"),sQuery(id+"F37.wireOp",EDGE,"E163.2.0"),sQuery(id+"F37.wireOp",EDGE,"E163.2.1")])]});
            var Q3;
            Q3=makeQuery(id+"F38.opExtrude","SWEPT_BODY",BODY,{"disambiguationData":[OSD([sQuery(id+"F37.wireOp",EDGE,"E156.0"),sQuery(id+"F37.wireOp",EDGE,"E157.0"),sQuery(id+"F37.wireOp",EDGE,"E163.1.0"),sQuery(id+"F37.wireOp",EDGE,"E163.1.1")])]});
            var Q4;
            Q4=makeQuery(id+"F24.opRevolve","SWEPT_BODY",BODY,{"disambiguationData":[OSD([sQuery(id+"F1.wireOp",EDGE,"E15.MirrorCS"),sQuery(id+"F1.wireOp",EDGE,"E16.MirrorCS"),sQuery(id+"F1.wireOp",EDGE,"E14.MirrorCS"),sQuery(id+"F1.wireOp",EDGE,"E17.MirrorCS"),sQuery(id+"F1.wireOp",EDGE,"E13"),sQuery(id+"F1.wireOp",EDGE,"E18.MirrorCS")])]});
            booleanBodies(context, id + "F39", {"operationType" : BooleanOperationType.UNION, "tools" : qUnion([Q0, Q1, Q2, Q3, Q4])});
        }
        {
            var Q0;
            {var subQ0=sQuery(id+"F37.wireOp",EDGE,"E157.0");var subQ1=sQuery(id+"F37.wireOp",EDGE,"E156.0");Q0=makeQuery(id+"F39.opBoolean","MERGE",FACE,{"derivedFrom":[makeQuery(id+"F5.opExtrude","CAP_FACE",FACE,{"disambiguationData":[OSD([sQuery(id+"F4.wireOp",EDGE,"E28"),sQuery(id+"F4.wireOp",EDGE,"E30")])],"isStart":true}),makeQuery(id+"F24.opRevolve","SWEPT_FACE",FACE,{"disambiguationData":[OSD([sQuery(id+"F1.wireOp",EDGE,"E17.MirrorCS")])]}),makeQuery(id+"F38.opExtrude","CAP_FACE",FACE,{"disambiguationData":[OSD([subQ1,subQ0,sQuery(id+"F37.wireOp",EDGE,"E163.1.0"),sQuery(id+"F37.wireOp",EDGE,"E163.1.1")])],"isStart":true}),makeQuery(id+"F38.opExtrude","CAP_FACE",FACE,{"disambiguationData":[OSD([subQ1,subQ0,sQuery(id+"F37.wireOp",EDGE,"E163.2.0"),sQuery(id+"F37.wireOp",EDGE,"E163.2.1")])],"isStart":true}),makeQuery(id+"F38.opExtrude","CAP_FACE",FACE,{"disambiguationData":[OSD([subQ1,subQ0,sQuery(id+"F37.wireOp",EDGE,"E160"),sQuery(id+"F37.wireOp",EDGE,"E161.MirrorCS")])],"isStart":true})]});}
            var sketch = newSketch(context, id + "F40", { "sketchPlane" : qUnion([Q0])});
            skArc(sketch, "E167.0", {"start": v(-14.27, -14.01) * mm, "mid": v(-19.27, 5.35) * mm, "end": v(-5, 19.36) * mm});
            skArc(sketch, "E168.0", {"start": v(-5, 19.36) * mm, "mid": v(14.27, 14.01) * mm, "end": v(19.27, -5.35) * mm});
            skArc(sketch, "E169.0", {"start": v(19.27, -5.35) * mm, "mid": v(5, -19.36) * mm, "end": v(-14.27, -14.01) * mm});
            skPoint(sketch, "E170.orphan", {"position": v(-19.27, -5.35) * mm});
            skPoint(sketch, "E171.orphan", {"position": v(14.27, -14.01) * mm});
            skPoint(sketch, "E172.orphan", {"position": v(5, 19.36) * mm});
            skArc(sketch, "E173.0", {"start": v(-4.75, 18.4) * mm, "mid": v(13.56, 13.31) * mm, "end": v(18.3, -5.08) * mm});
            skArc(sketch, "E173.1", {"start": v(-13.56, -13.31) * mm, "mid": v(-18.3, 5.08) * mm, "end": v(-4.75, 18.4) * mm});
            skArc(sketch, "E173.2", {"start": v(18.3, -5.08) * mm, "mid": v(4.75, -18.4) * mm, "end": v(-13.56, -13.31) * mm});
            skArc(sketch, "E174.0", {"start": v(-7.34, 1.54) * mm, "mid": v(-6.5, 3.75) * mm, "end": v(-5, 5.6) * mm});
            skCircle(sketch, "E175", {"center": v(0, 0) * mm, "radius": 7.5 * mm});
            skCircle(sketch, "E176", {"center": v(0, 0) * mm, "radius": 8.5 * mm});
            skSolve(sketch);
        }
        {
            var Q0;
            {var subQ0=sQuery(id+"F40.wireOp",EDGE,"E168.0");var subQ1=makeQuery(id+"F38.opExtrude","CAP_EDGE",EDGE,{"disambiguationData":[OSD([sQuery(id+"F37.wireOp",EDGE,"E164")])],"isStart":true});var subQ2=makeQuery(id+"F40.imprint","INTERSECT",VERTEX,{"derivedFrom":[subQ1,subQ0]});Q0=makeQuery(id+"F40.imprint","IMPRINT",FACE,{"disambiguationData":[TD([[makeQuery(id+"F40.imprint","IMPRINT",EDGE,{"disambiguationData":[TD([[subQ2,1.0]])],"derivedFrom":subQ0}),-1.0]])]});}
            var Q1;
            {var subQ0=sQuery(id+"F40.wireOp",EDGE,"E167.0");var subQ1=makeQuery(id+"F38.opExtrude","CAP_EDGE",EDGE,{"disambiguationData":[OSD([sQuery(id+"F37.wireOp",EDGE,"E166.2.0")])],"isStart":true});var subQ2=makeQuery(id+"F40.imprint","INTERSECT",VERTEX,{"derivedFrom":[subQ1,subQ0]});Q1=makeQuery(id+"F40.imprint","IMPRINT",FACE,{"disambiguationData":[TD([[makeQuery(id+"F40.imprint","IMPRINT",EDGE,{"disambiguationData":[TD([[subQ2,-1.0]])],"derivedFrom":subQ0}),-1.0]])]});}
            var Q2;
            {var subQ0=sQuery(id+"F40.wireOp",EDGE,"E169.0");var subQ1=makeQuery(id+"F38.opExtrude","CAP_EDGE",EDGE,{"disambiguationData":[OSD([sQuery(id+"F37.wireOp",EDGE,"E166.1.0")])],"isStart":true});var subQ2=makeQuery(id+"F40.imprint","INTERSECT",VERTEX,{"derivedFrom":[subQ1,subQ0]});Q2=makeQuery(id+"F40.imprint","IMPRINT",FACE,{"disambiguationData":[TD([[makeQuery(id+"F40.imprint","IMPRINT",EDGE,{"disambiguationData":[TD([[subQ2,-1.0]])],"derivedFrom":subQ0}),-1.0]])]});}
            var Q3;
            {var subQ0=sQuery(id+"F40.wireOp",EDGE,"E175");var subQ1=makeQuery(id+"F38.opExtrude","CAP_EDGE",EDGE,{"disambiguationData":[OSD([sQuery(id+"F37.wireOp",EDGE,"E166.2.0")])],"isStart":true});var subQ2=makeQuery(id+"F40.imprint","INTERSECT",VERTEX,{"derivedFrom":[subQ1,subQ0]});var subQ3=makeQuery(id+"F38.opExtrude","CAP_EDGE",EDGE,{"disambiguationData":[OSD([sQuery(id+"F37.wireOp",EDGE,"E166.2.1")])],"isStart":true});var subQ4=makeQuery(id+"F40.imprint","INTERSECT",VERTEX,{"derivedFrom":[subQ3,subQ0]});Q3=makeQuery(id+"F40.imprint","IMPRINT",FACE,{"disambiguationData":[TD([[makeQuery(id+"F40.imprint","IMPRINT",EDGE,{"disambiguationData":[TD([[subQ2,1.0],[subQ4,-1.0]])],"derivedFrom":subQ0}),-1.0]])]});}
            var Q4;
            {var subQ0=sQuery(id+"F40.wireOp",EDGE,"E175");var subQ1=makeQuery(id+"F38.opExtrude","CAP_EDGE",EDGE,{"disambiguationData":[OSD([sQuery(id+"F37.wireOp",EDGE,"E164")])],"isStart":true});var subQ2=makeQuery(id+"F40.imprint","INTERSECT",VERTEX,{"derivedFrom":[subQ1,subQ0]});var subQ3=makeQuery(id+"F38.opExtrude","CAP_EDGE",EDGE,{"disambiguationData":[OSD([sQuery(id+"F37.wireOp",EDGE,"E165.MirrorCS")])],"isStart":true});var subQ4=makeQuery(id+"F40.imprint","INTERSECT",VERTEX,{"derivedFrom":[subQ3,subQ0]});Q4=makeQuery(id+"F40.imprint","IMPRINT",FACE,{"disambiguationData":[TD([[makeQuery(id+"F40.imprint","IMPRINT",EDGE,{"disambiguationData":[TD([[subQ2,-1.0],[subQ4,1.0]])],"derivedFrom":subQ0}),-1.0]])]});}
            var Q5;
            {var subQ0=sQuery(id+"F40.wireOp",EDGE,"E175");var subQ1=makeQuery(id+"F38.opExtrude","CAP_EDGE",EDGE,{"disambiguationData":[OSD([sQuery(id+"F37.wireOp",EDGE,"E166.1.0")])],"isStart":true});var subQ2=makeQuery(id+"F40.imprint","INTERSECT",VERTEX,{"derivedFrom":[subQ1,subQ0]});var subQ3=makeQuery(id+"F38.opExtrude","CAP_EDGE",EDGE,{"disambiguationData":[OSD([sQuery(id+"F37.wireOp",EDGE,"E166.1.1")])],"isStart":true});var subQ4=makeQuery(id+"F40.imprint","INTERSECT",VERTEX,{"derivedFrom":[subQ3,subQ0]});Q5=makeQuery(id+"F40.imprint","IMPRINT",FACE,{"disambiguationData":[TD([[makeQuery(id+"F40.imprint","IMPRINT",EDGE,{"disambiguationData":[TD([[subQ2,1.0],[subQ4,-1.0]])],"derivedFrom":subQ0}),-1.0]])]});}
            extrude(context, id + "F41", {"entities" : qUnion([Q0, Q1, Q2, Q3, Q4, Q5]), "operationType" : NewBodyOperationType.REMOVE, "oppositeDirection" : true, "depth" : 1 * mm, "offsetDistance" : 25 * mm});
        }
        {
            var Q0;
            {var subQ0=sQuery(id+"F18.wireOp",EDGE,"E135");var subQ1=sQuery(id+"F18.wireOp",EDGE,"E134");var subQ2=sQuery(id+"F18.wireOp",EDGE,"E131");var subQ3=sQuery(id+"F16.wireOp",EDGE,"E124");var subQ4=sQuery(id+"F16.wireOp",EDGE,"E123");var subQ5=sQuery(id+"F16.wireOp",EDGE,"E120");var subQ6=makeQuery(id+"F21.opBoolean","MERGE",FACE,{"derivedFrom":[makeQuery(id+"F19.opExtrude","CAP_FACE",FACE,{"disambiguationData":[OSD([subQ5,subQ4,subQ3,sQuery(id+"F18.wireOp",EDGE,"E130"),subQ2,subQ1,subQ0])],"isStart":true}),makeQuery(id+"F20.opExtrude","CAP_FACE",FACE,{"disambiguationData":[OSD([subQ5,subQ4,subQ3,sQuery(id+"F18.wireOp",EDGE,"E129"),subQ2,subQ1,subQ0])],"isStart":true})]});Q0=makeQuery(id+"F23.opBoolean","MERGE",FACE,{"derivedFrom":[makeQuery(id+"F17.opRevolve","SWEPT_FACE",FACE,{"disambiguationData":[OSD([subQ5])]}),subQ6,makeQuery(id+"F22.opPattern","COPY",FACE,{"derivedFrom":subQ6,"instanceName":"1"})]});}
            var sketch = newSketch(context, id + "F42", { "sketchPlane" : qUnion([Q0])});
            skCircle(sketch, "E177", {"center": v(-17.1, 0) * mm, "radius": 1.5 * mm});
            skCircle(sketch, "E178", {"center": v(17.1, 0) * mm, "radius": 1.5 * mm});
            skLineSegment(sketch, "E179.0", {"start": v(-17.1, -5.25) * mm, "end": v(-12, -5.25) * mm, "construction": true});
            skArc(sketch, "E180.0.0", {"start": v(-12, -5.25) * mm, "mid": v(0, -13.1) * mm, "end": v(12, -5.25) * mm});
            skLineSegment(sketch, "E180.0.1", {"start": v(12, -5.25) * mm, "end": v(17.1, -5.25) * mm, "construction": true});
            skArc(sketch, "E180.0.2", {"start": v(17.1, -5.25) * mm, "mid": v(22.35, 0) * mm, "end": v(17.1, 5.25) * mm});
            skLineSegment(sketch, "E180.0.3", {"start": v(17.1, 5.25) * mm, "end": v(12, 5.25) * mm, "construction": true});
            skArc(sketch, "E180.0.4", {"start": v(12, 5.25) * mm, "mid": v(0, 13.1) * mm, "end": v(-12, 5.25) * mm, "construction": true});
            skLineSegment(sketch, "E180.0.5", {"start": v(-12, 5.25) * mm, "end": v(-17.1, 5.25) * mm, "construction": true});
            skArc(sketch, "E180.0.6", {"start": v(-17.1, 5.25) * mm, "mid": v(-22.35, 0) * mm, "end": v(-17.1, -5.25) * mm});
            skLineSegment(sketch, "E181", {"start": v(-17.1, -5.25) * mm, "end": v(17.1, -5.25) * mm});
            skLineSegment(sketch, "E182", {"start": v(-22.35, 0) * mm, "end": v(-22.35, 25) * mm});
            skLineSegment(sketch, "E183", {"start": v(-22.35, 25) * mm, "end": v(22.35, 25) * mm});
            skPoint(sketch, "E183.endSnap0", {"position": v(22.35, 0) * mm});
            skLineSegment(sketch, "E184", {"start": v(22.35, 25) * mm, "end": v(22.35, 0) * mm});
            skCircle(sketch, "E185", {"center": v(0, 0) * mm, "radius": 7 * mm});
            skSolve(sketch);
        }
        {
            var Q0;
            {var subQ9=sQuery(id+"F18.wireOp",EDGE,"E130");var subQ27=makeQuery(id+"F19.opExtrude","CAP_EDGE",EDGE,{"disambiguationData":[OSD([subQ9])],"isStart":true});Q0=makeQuery(id+"F42.imprint","IMPRINT",FACE,{"disambiguationData":[TD([[makeQuery(id+"F42.imprint","IMPRINT",EDGE,{"derivedFrom":subQ27}),-1.0]])]});}
            var Q1;
            {var subQ0=sQuery(id+"F42.wireOp",EDGE,"E182");Q1=makeQuery(id+"F42.imprint","IMPRINT",FACE,{"disambiguationData":[TD([[makeQuery(id+"F42.imprint","IMPRINT",EDGE,{"derivedFrom":subQ0}),-1.0]])]});}
            var Q2;
            {var subQ0=sQuery(id+"F42.wireOp",EDGE,"E181");var subQ1=makeQuery(id+"F17.opRevolve","SWEPT_EDGE",EDGE,{"disambiguationData":[OSD([sQuery(id+"F16.wireOp",EDGE,"E119"),sQuery(id+"F16.wireOp",EDGE,"E120")])]});var subQ2=makeQuery(id+"F42.imprint","INTERSECT",VERTEX,{"disambiguationData":[OD(0.0)],"derivedFrom":[subQ1,subQ0]});Q2=makeQuery(id+"F42.imprint","IMPRINT",FACE,{"disambiguationData":[TD([[makeQuery(id+"F42.imprint","IMPRINT",EDGE,{"disambiguationData":[TD([[subQ2,-1.0]])],"derivedFrom":subQ0}),1.0]])]});}
            var Q3;
            {var subQ0=sQuery(id+"F42.wireOp",EDGE,"rXZswB1A-rXHv-fHct-yRDe-tseMWWbPkpxh");var subQ1=sQuery(id+"F42.wireOp",EDGE,"E181");var subQ2=makeQuery(id+"F42.imprint","INTERSECT",VERTEX,{"disambiguationData":[OD(0.0)],"derivedFrom":[subQ1,subQ0]});Q3=makeQuery(id+"F42.imprint","IMPRINT",FACE,{"disambiguationData":[TD([[makeQuery(id+"F42.imprint","IMPRINT",EDGE,{"disambiguationData":[TD([[subQ2,-1.0]])],"derivedFrom":subQ1}),1.0]])]});}
            var Q4;
            {var subQ0=sQuery(id+"F42.wireOp",EDGE,"E185");var subQ1=sQuery(id+"F42.wireOp",EDGE,"E181");var subQ2=makeQuery(id+"F42.imprint","INTERSECT",VERTEX,{"disambiguationData":[OD(0.0)],"derivedFrom":[subQ1,subQ0]});Q4=makeQuery(id+"F42.imprint","IMPRINT",FACE,{"disambiguationData":[TD([[makeQuery(id+"F42.imprint","IMPRINT",EDGE,{"disambiguationData":[TD([[subQ2,-1.0]])],"derivedFrom":subQ0}),-1.0]])]});}
            var Q5;
            {var subQ0=sQuery(id+"F42.wireOp",EDGE,"E181");var subQ6=sQuery(id+"F16.wireOp",EDGE,"E120");var subQ10=makeQuery(id+"F17.opRevolve","SWEPT_EDGE",EDGE,{"disambiguationData":[OSD([sQuery(id+"F16.wireOp",EDGE,"E119"),subQ6])]});var subQ11=makeQuery(id+"F42.imprint","INTERSECT",VERTEX,{"disambiguationData":[OD(0.0)],"derivedFrom":[subQ10,subQ0]});Q5=makeQuery(id+"F42.imprint","IMPRINT",FACE,{"disambiguationData":[TD([[makeQuery(id+"F42.imprint","IMPRINT",EDGE,{"disambiguationData":[TD([[subQ11,-1.0]])],"derivedFrom":subQ10}),-1.0]])]});}
            var Q6;
            {var subQ0=sQuery(id+"F42.wireOp",EDGE,"E181");var subQ10=sQuery(id+"F42.wireOp",EDGE,"rXZswB1A-rXHv-fHct-yRDe-tseMWWbPkpxh");var subQ11=makeQuery(id+"F42.imprint","INTERSECT",VERTEX,{"disambiguationData":[OD(0.0)],"derivedFrom":[subQ0,subQ10]});Q6=makeQuery(id+"F42.imprint","IMPRINT",FACE,{"disambiguationData":[TD([[makeQuery(id+"F42.imprint","IMPRINT",EDGE,{"disambiguationData":[TD([[subQ11,-1.0]])],"derivedFrom":subQ10}),1.0]])]});}
            var Q7;
            Q7=makeQuery(id+"F42.imprint","IMPRINT",FACE,{"disambiguationData":[TD([[makeQuery(id+"F42.imprint","IMPRINT",EDGE,{"derivedFrom":makeQuery(id+"F22.opPattern","COPY",EDGE,{"derivedFrom":makeQuery(id+"F19.opExtrude","CAP_EDGE",EDGE,{"disambiguationData":[OSD([sQuery(id+"F18.wireOp",EDGE,"E130")])],"isStart":true}),"instanceName":"1"})}),-1.0]])]});
            var Q8;
            {var subQ0=sQuery(id+"F42.wireOp",EDGE,"rXZswB1A-rXHv-fHct-yRDe-tseMWWbPkpxh");var subQ1=sQuery(id+"F18.wireOp",EDGE,"E135");var subQ2=makeQuery(id+"F20.opExtrude","CAP_EDGE",EDGE,{"disambiguationData":[OSD([subQ1])],"isStart":true});var subQ3=makeQuery(id+"F42.imprint","INTERSECT",VERTEX,{"derivedFrom":[subQ2,subQ0]});Q8=makeQuery(id+"F42.imprint","IMPRINT",FACE,{"disambiguationData":[TD([[makeQuery(id+"F42.imprint","IMPRINT",EDGE,{"disambiguationData":[TD([[subQ3,1.0]])],"derivedFrom":subQ0}),1.0]])]});}
            var Q9;
            Q9=makeQuery(id+"F42.imprint","IMPRINT",FACE,{"disambiguationData":[TD([[makeQuery(id+"F42.imprint","IMPRINT",EDGE,{"derivedFrom":sQuery(id+"F42.wireOp",EDGE,"E177")}),-1.0]])]});
            var Q10;
            Q10=makeQuery(id+"F42.imprint","IMPRINT",FACE,{"disambiguationData":[TD([[makeQuery(id+"F42.imprint","IMPRINT",EDGE,{"derivedFrom":sQuery(id+"F42.wireOp",EDGE,"E178")}),-1.0]])]});
            extrude(context, id + "F43", {"entities" : qUnion([Q0, Q1, Q2, Q3, Q4, Q5, Q6, Q7, Q8, Q9, Q10]), "depth" : 3 * mm, "offsetDistance" : 25 * mm});
        }
        {
            var Q0;
            Q0=qCreatedBy(makeId("Right.planeOp"),FACE);
            var sketch = newSketch(context, id + "F44", { "sketchPlane" : qUnion([Q0])});
            skLineSegment(sketch, "E186", {"start": v(-23, 15) * mm, "end": v(-23, 25) * mm, "construction": true});
            skLineSegment(sketch, "E187", {"start": v(23, 25) * mm, "end": v(23, 15) * mm});
            skLineSegment(sketch, "E188", {"start": v(-25, 25) * mm, "end": v(-25, 30) * mm, "construction": true});
            skLineSegment(sketch, "E189", {"start": v(25, 30) * mm, "end": v(25, 25) * mm});
            skLineSegment(sketch, "E190.0.0", {"start": v(25, 25) * mm, "end": v(-25, 25) * mm, "construction": true});
            skLineSegment(sketch, "E191.0.0", {"start": v(-25, 5) * mm, "end": v(25, 5) * mm, "construction": true});
            skLineSegment(sketch, "E192", {"start": v(23, 15) * mm, "end": v(23, 5) * mm});
            skLineSegment(sketch, "E193", {"start": v(-23, 5) * mm, "end": v(-23, 15) * mm, "construction": true});
            skLineSegment(sketch, "E194", {"start": v(-25, 0) * mm, "end": v(-25, 5) * mm, "construction": true});
            skLineSegment(sketch, "E195.0.0", {"start": v(25, 0) * mm, "end": v(-25, 0) * mm, "construction": true});
            skLineSegment(sketch, "E196.0.0", {"start": v(-25, 30) * mm, "end": v(25, 30) * mm, "construction": true});
            skLineSegment(sketch, "E197", {"start": v(25, 25) * mm, "end": v(23, 25) * mm});
            skLineSegment(sketch, "E198", {"start": v(23, 5) * mm, "end": v(25, 5) * mm});
            skLineSegment(sketch, "E199", {"start": v(25, 30) * mm, "end": v(25, 31) * mm});
            skLineSegment(sketch, "E200", {"start": v(25, 31) * mm, "end": v(28, 31) * mm});
            skLineSegment(sketch, "E201", {"start": v(25, 5) * mm, "end": v(25, 0) * mm});
            skLineSegment(sketch, "E202", {"start": v(25, 0) * mm, "end": v(25, -1) * mm});
            skLineSegment(sketch, "E203", {"start": v(25, -1) * mm, "end": v(28, -1) * mm});
            skLineSegment(sketch, "E204", {"start": v(28, -1) * mm, "end": v(28, 31) * mm});
            skLineSegment(sketch, "E205", {"start": v(28, 15) * mm, "end": v(28, 31) * mm, "construction": true});
            skLineSegment(sketch, "E206", {"start": v(28, 15) * mm, "end": v(23, 15) * mm, "construction": true});
            skLineSegment(sketch, "E207", {"start": v(28, 23) * mm, "end": v(30.5, 23) * mm, "construction": true});
            skCircle(sketch, "E208", {"center": v(30.5, 23) * mm, "radius": 3.5 * mm});
            skCircle(sketch, "E209.MirrorC", {"center": v(30.5, 7) * mm, "radius": 3.5 * mm});
            skLineSegment(sketch, "E210.MirrorCS", {"start": v(28, 7) * mm, "end": v(30.5, 7) * mm, "construction": true});
            skLineSegment(sketch, "E211", {"start": v(23, 20) * mm, "end": v(23, 25) * mm, "construction": true});
            skLineSegment(sketch, "E212", {"start": v(23, 10) * mm, "end": v(23, 5) * mm, "construction": true});
            skArc(sketch, "E213", {"start": v(23, 7.5) * mm, "mid": v(26.39, 15) * mm, "end": v(23, 22.5) * mm});
            skSolve(sketch);
        }
        {
            var Q0;
            Q0=makeQuery(id+"F44.imprint","IMPRINT",FACE,{"disambiguationData":[TD([[makeQuery(id+"F44.imprint","IMPRINT",EDGE,{"derivedFrom":sQuery(id+"F44.wireOp",EDGE,"E189")}),1.0]])]});
            var Q1;
            Q1=makeQuery(id+"F41.boolean.opBoolean","MERGE",FACE,{"derivedFrom":[makeQuery(id+"F25.opBoolean","MERGE",FACE,{"derivedFrom":[makeQuery(id+"F24.opRevolve","SWEPT_FACE",FACE,{"disambiguationData":[OSD([sQuery(id+"F1.wireOp",EDGE,"E18.MirrorCS")])]}),makeQuery(id+"F24.opRevolve","SWEPT_FACE",FACE,{"disambiguationData":[OSD([sQuery(id+"F2.wireOp",EDGE,"E21")])]})]}),makeQuery(id+"F41.opExtrude","SWEPT_FACE",FACE,{"disambiguationData":[OSD([sQuery(id+"F40.wireOp",EDGE,"E167.0")])]}),makeQuery(id+"F41.opExtrude","SWEPT_FACE",FACE,{"disambiguationData":[OSD([sQuery(id+"F40.wireOp",EDGE,"E168.0")])]}),makeQuery(id+"F41.opExtrude","SWEPT_FACE",FACE,{"disambiguationData":[OSD([sQuery(id+"F40.wireOp",EDGE,"E169.0")])]})]});
            revolve(context, id + "F45", {"entities" : qUnion([Q0]), "axis" : qUnion([Q1]), "revolveType" : RevolveType.FULL});
        }
        {
            var Q0;
            Q0=makeQuery(id+"F17.opRevolve","SWEPT_EDGE",EDGE,{"disambiguationData":[OSD([sQuery(id+"F16.wireOp",EDGE,"E119"),sQuery(id+"F16.wireOp",EDGE,"E120")])]});
            fillet(context, id + "F46", {"entities" : qUnion([Q0]), "radius" : 1 * mm, "tangentPropagation" : true, "allowEdgeOverflow" : false});
        }
    });
